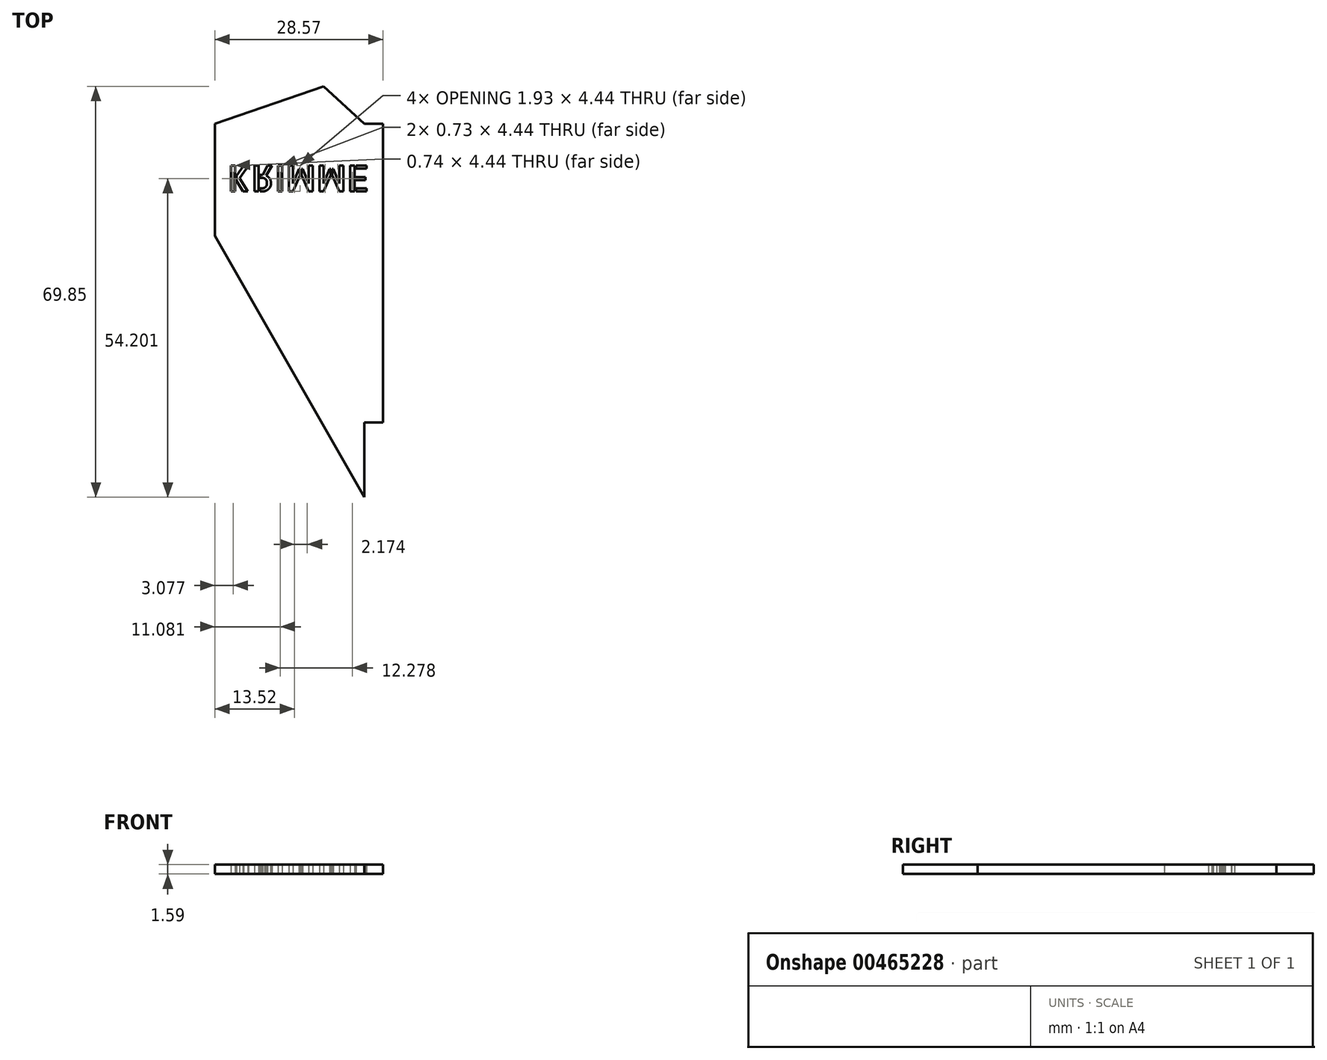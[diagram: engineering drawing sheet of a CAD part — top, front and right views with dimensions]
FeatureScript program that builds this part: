
annotation { "Feature Type Name" : "Feature", "Feature Type Description" : "" }
export const myFeature = defineFeature(function(context is Context, id is Id, definition is map)
    precondition{}
    {
        {
            var Q0;
            Q0=qCreatedBy(makeId("Top.planeOp"),FACE);
            var sketch = newSketch(context, id + "F0", { "sketchPlane" : qUnion([Q0])});
            skLineSegment(sketch, "E0", {"start": v(-31.33, 24.7) * mm, "end": v(-31.33, 5.66) * mm});
            skLineSegment(sketch, "E1", {"start": v(-5.93, 24.7) * mm, "end": v(-2.76, 24.7) * mm});
            skLineSegment(sketch, "E2", {"start": v(-2.76, 24.7) * mm, "end": v(-2.76, -26.1) * mm});
            skLineSegment(sketch, "E3", {"start": v(-2.76, -26.1) * mm, "end": v(-5.93, -26.1) * mm});
            skLineSegment(sketch, "E4", {"start": v(-5.93, -26.1) * mm, "end": v(-5.93, -38.8) * mm});
            skLineSegment(sketch, "E5", {"start": v(-5.93, -38.8) * mm, "end": v(-31.33, 5.66) * mm});
            skLineSegment(sketch, "E6", {"start": v(-31.33, 24.7) * mm, "end": v(-12.85, 31.06) * mm});
            skLineSegment(sketch, "E7", {"start": v(-12.85, 31.06) * mm, "end": v(-5.93, 24.7) * mm});
            skPoint(sketch, "E8.end.orphan", {"position": v(-31.33, 31.06) * mm});
            skSolve(sketch);
        }
        {
            var Q0;
            Q0=makeQuery(id+"F0.imprint","IMPRINT",FACE,{"disambiguationData":[TD([[makeQuery(id+"F0.imprint","IMPRINT",EDGE,{"derivedFrom":sQuery(id+"F0.wireOp",EDGE,"E0")}),1.0]])]});
            extrude(context, id + "F1", {"entities" : qUnion([Q0]), "depth" : 1.59 * mm});
        }
        {
            var Q0;
            Q0=makeQuery(id+"F1.opExtrude","CAP_FACE",FACE,{"disambiguationData":[OSD([sQuery(id+"F0.wireOp",EDGE,"E0"),sQuery(id+"F0.wireOp",EDGE,"E1"),sQuery(id+"F0.wireOp",EDGE,"E2"),sQuery(id+"F0.wireOp",EDGE,"E3"),sQuery(id+"F0.wireOp",EDGE,"E4"),sQuery(id+"F0.wireOp",EDGE,"E5"),sQuery(id+"F0.wireOp",EDGE,"E6"),sQuery(id+"F0.wireOp",EDGE,"E7")])],"isStart":true});
            var sketch = newSketch(context, id + "F2", { "sketchPlane" : qUnion([Q0])});
            skText(sketch, "E9", { "text": "KRIMME", "fontName": "AllertaStencil-Regular.ttf"});
            const initialGuessF2  = {"E9": [-0.02918, -0.01763, 1, 0, 0.00444]};
            skSetInitialGuess(sketch, initialGuessF2);
            skSolve(sketch);
        }
        {
            var Q0;
            Q0 = qSketchRegion(id + "F2", true);
            extrude(context, id + "F3", {"entities" : qUnion([Q0]), "operationType" : NewBodyOperationType.REMOVE, "endBound" : BoundingType.THROUGH_ALL, "oppositeDirection" : true, "depth" : 25.4 * mm});
        }
    });
